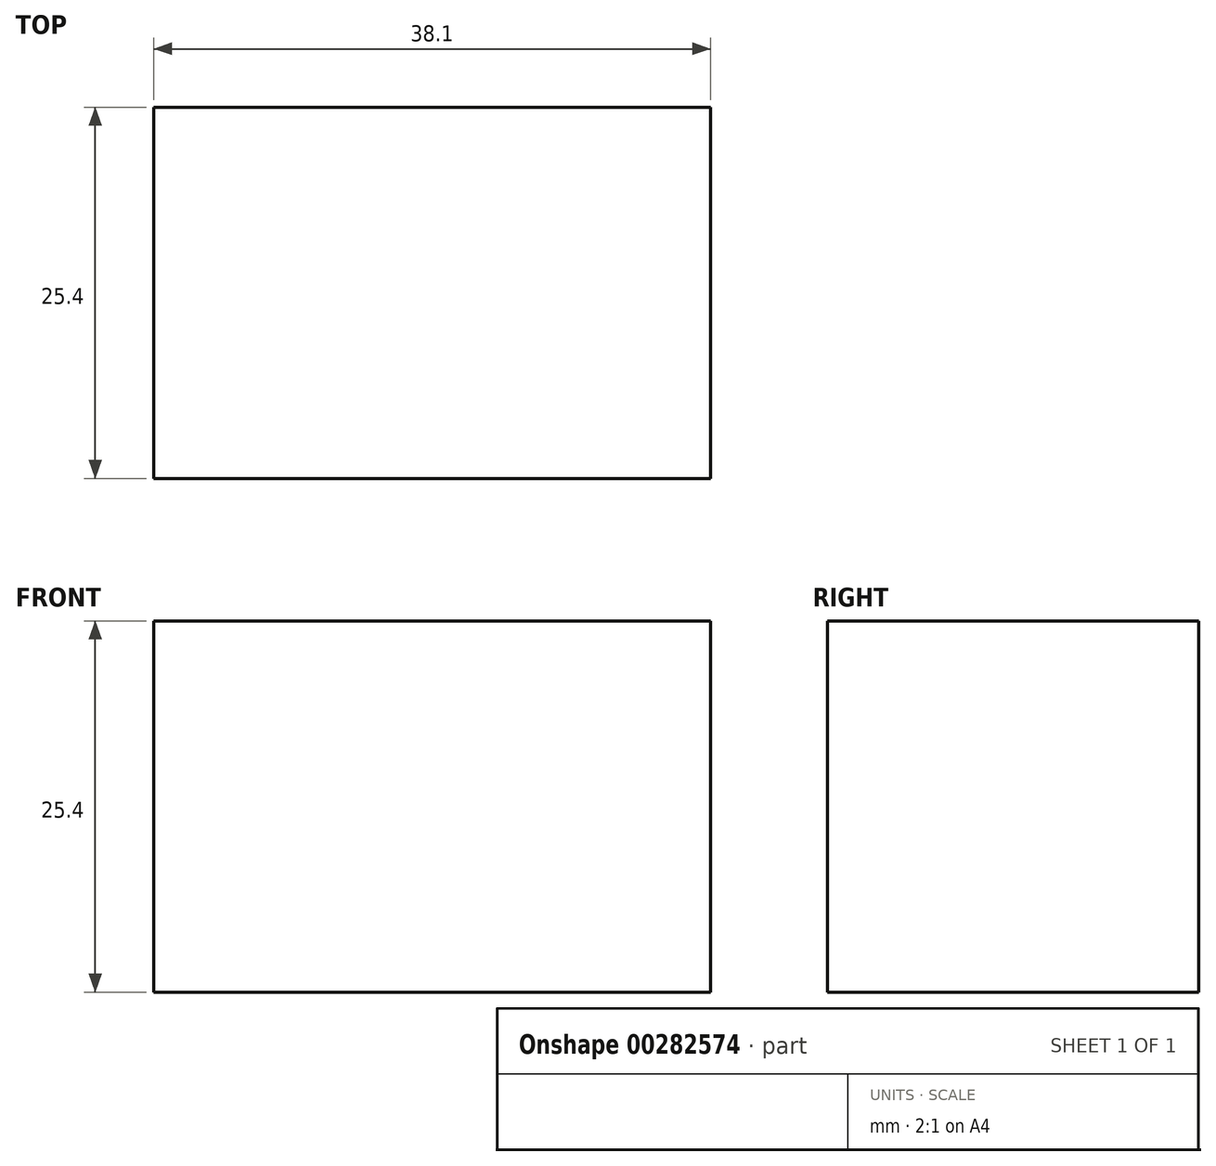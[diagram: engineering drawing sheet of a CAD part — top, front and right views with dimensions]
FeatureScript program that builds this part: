
annotation { "Feature Type Name" : "Feature", "Feature Type Description" : "" }
export const myFeature = defineFeature(function(context is Context, id is Id, definition is map)
    precondition{}
    {
        {
            var Q0;
            Q0=qCreatedBy(makeId("Front.planeOp"),FACE);
            var sketch = newSketch(context, id + "F0", { "sketchPlane" : qUnion([Q0])});
            skLineSegment(sketch, "E0", {"start": v(0, 0) * mm, "end": v(0, 25.4) * mm});
            skLineSegment(sketch, "E1", {"start": v(0, 25.4) * mm, "end": v(-38.1, 25.4) * mm});
            skLineSegment(sketch, "E2", {"start": v(-38.1, 25.4) * mm, "end": v(-38.1, 0) * mm});
            skLineSegment(sketch, "E3", {"start": v(-38.1, 0) * mm, "end": v(0, 0) * mm});
            skLineSegment(sketch, "E4", {"start": v(-19.05, 25.4) * mm, "end": v(0, 6.35) * mm});
            skSolve(sketch);
        }
        {
            var Q0;
            {var subQ0=sQuery(id+"F0.wireOp",EDGE,"E2");Q0=makeQuery(id+"F0.imprint","IMPRINT",FACE,{"disambiguationData":[TD([[makeQuery(id+"F0.imprint","IMPRINT",EDGE,{"derivedFrom":subQ0}),1.0]])]});}
            var Q1;
            {var subQ3=sQuery(id+"F0.wireOp",EDGE,"E4");Q1=makeQuery(id+"F0.imprint","IMPRINT",FACE,{"disambiguationData":[TD([[makeQuery(id+"F0.imprint","IMPRINT",EDGE,{"derivedFrom":subQ3}),1.0]])]});}
            extrude(context, id + "F1", {"entities" : qUnion([Q0, Q1]), "endBound" : BoundingType.SYMMETRIC, "depth" : 25.4 * mm});
        }
    });
